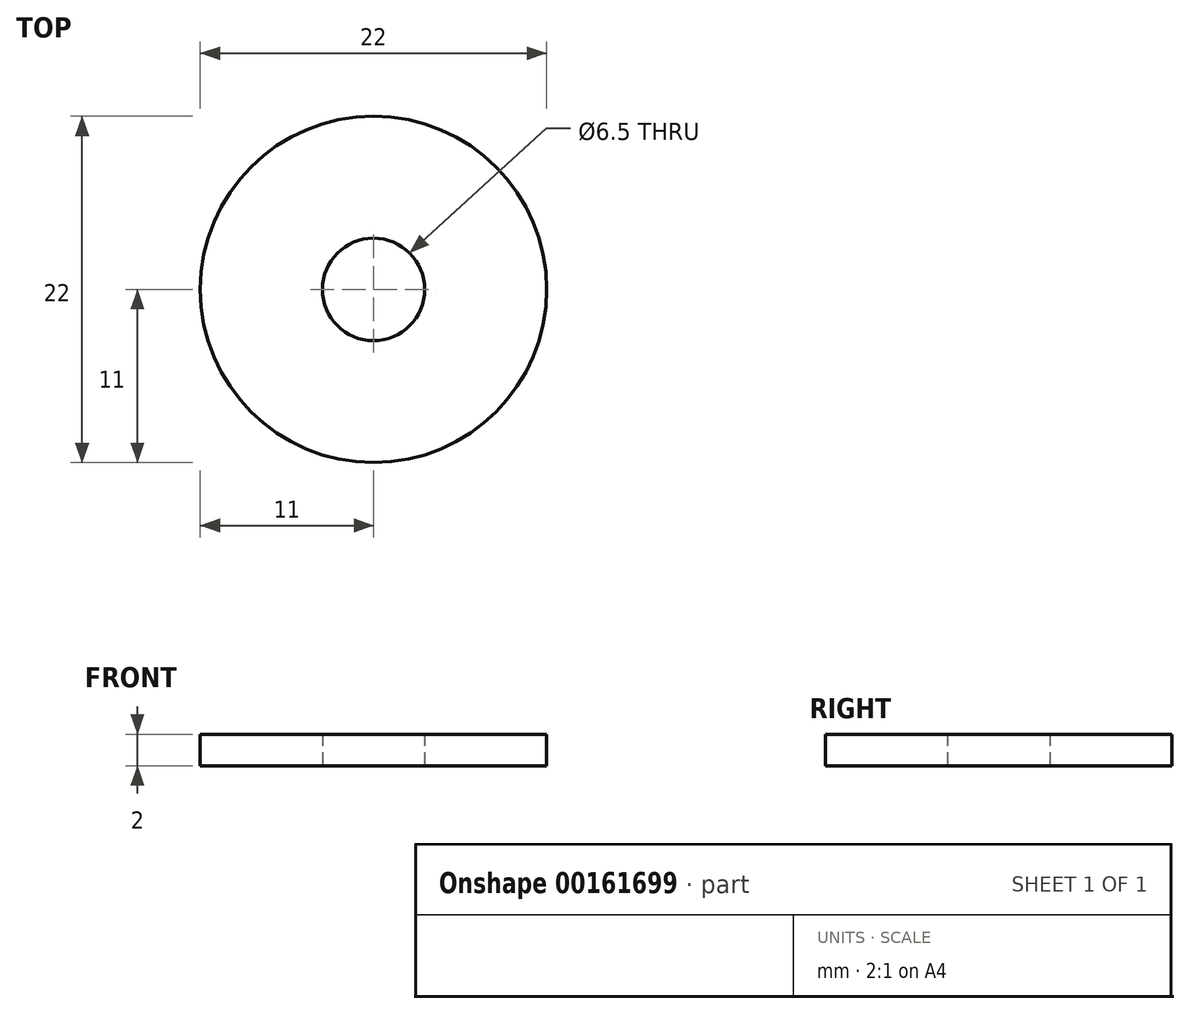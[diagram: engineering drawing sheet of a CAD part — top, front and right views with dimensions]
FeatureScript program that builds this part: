
annotation { "Feature Type Name" : "Feature", "Feature Type Description" : "" }
export const myFeature = defineFeature(function(context is Context, id is Id, definition is map)
    precondition{}
    {
        {
            var Q0;
            Q0=qCreatedBy(makeId("Top.planeOp"),FACE);
            var sketch = newSketch(context, id + "F0", { "sketchPlane" : qUnion([Q0])});
            skCircle(sketch, "E0", {"center": v(0, 0) * mm, "radius": 3.25 * mm});
            skCircle(sketch, "E1", {"center": v(0, 0) * mm, "radius": 11 * mm});
            skSolve(sketch);
        }
        {
            var Q0;
            Q0=makeQuery(id+"F0.imprint","IMPRINT",FACE,{"disambiguationData":[TD([[makeQuery(id+"F0.imprint","IMPRINT",EDGE,{"derivedFrom":sQuery(id+"F0.wireOp",EDGE,"E0")}),-1.0]])]});
            extrude(context, id + "F1", {"entities" : qUnion([Q0]), "depth" : 2 * mm});
        }
    });
